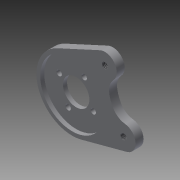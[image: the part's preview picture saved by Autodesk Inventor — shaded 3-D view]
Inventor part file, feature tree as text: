
AUTODESK INVENTOR PART (.ipt)
format: ipt  version: 2015 (Build 190159000, 159)  size: 159,232 bytes
history: native  units: in
note: dims shown in document units (in); Inventor stores cm internally (conversion verified against a paired STEP export)
features: extrude x3, sketch x2, thread x2, other x1, fillet x1, projected_geometry x1
ambient origin geometry x8: Origin, YZ Plane, XZ Plane, XY Plane, X Axis, Y Axis, Z Axis, Center Point
bodies: Solid1 (feature_tree)
feature tree (10):
  other  "mount_sketch.ipt"
  extrude  "Extrusion1"  Depth=0.25in TaperAngle=0.0deg
  fillet  "Fillet1"  Radius=0.5in
  sketch  "Sketch3"  dims[d4=2.0079in d5=0.1181in d6=0.0in d7=0.0in d8=0.125in d9=0.0in d10=1.0in d11=0.0in d12=1.0in d13=0.0in]
  extrude  "Extrusion2"  Depth=0.125in
  extrude  "Extrusion3"  TaperAngle=0.0deg  [1 undecoded]
  thread  "Thread1"  [1 undecoded]
  thread  "Thread2"  [1 undecoded]
  sketch  "Sketch2"  dims[d0=0.3937in d1=0.25in d2=0.0in d3=0.5in]
  projected_geometry  "Projected Loop1"
note: 3 required parameter values undecoded (feature->parameter linkage not recoverable at this tier; creation-order binding heuristic only, values carry confidence <= 0.55)
